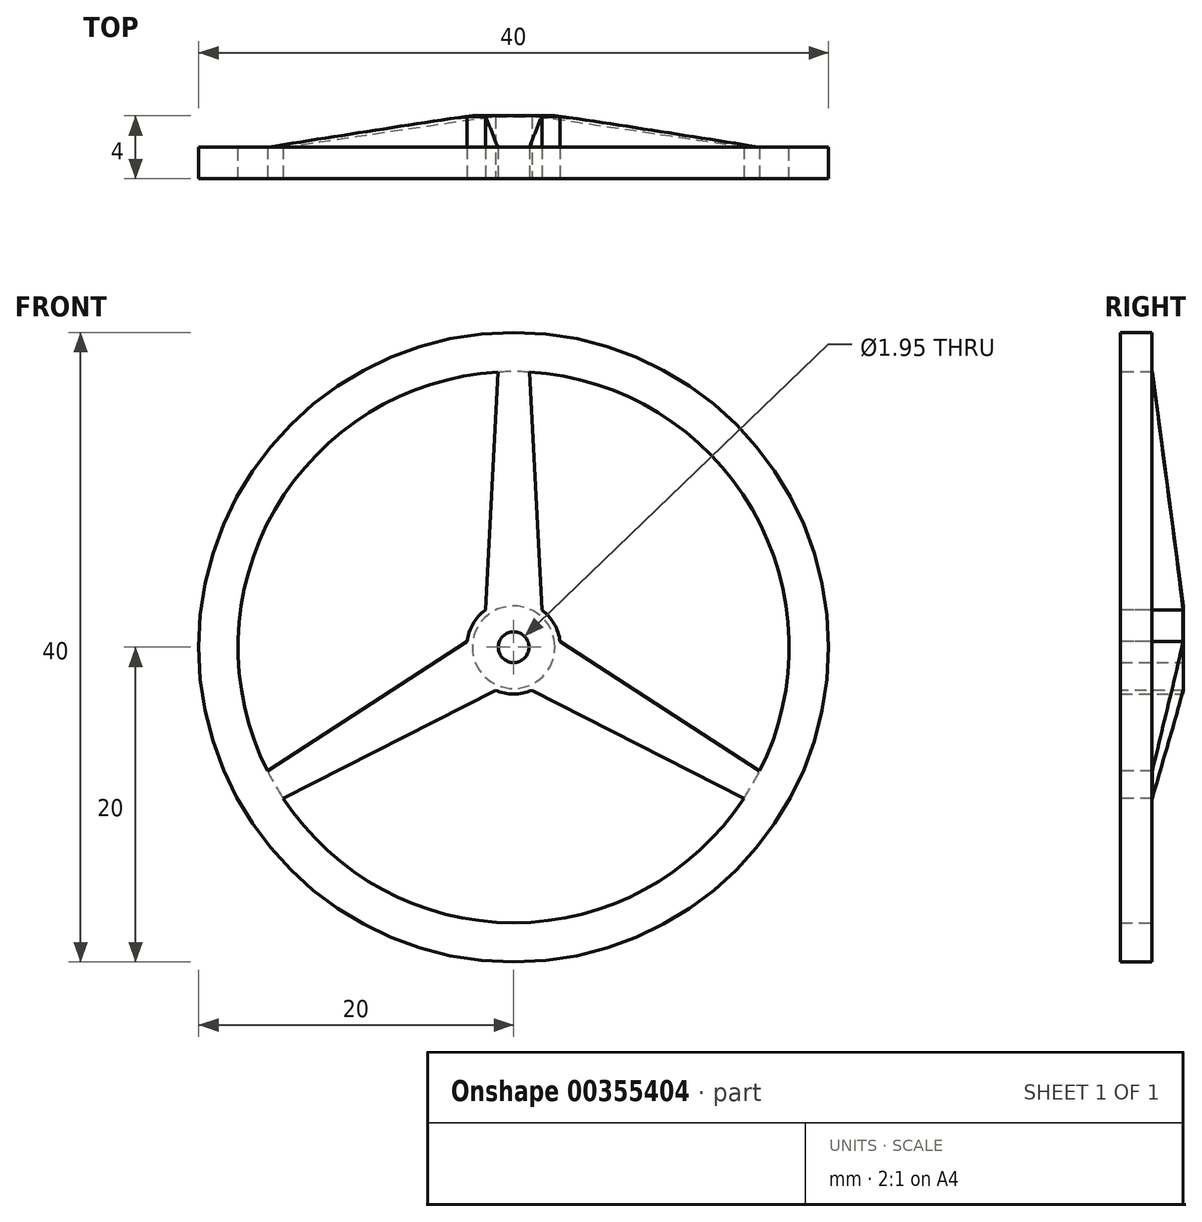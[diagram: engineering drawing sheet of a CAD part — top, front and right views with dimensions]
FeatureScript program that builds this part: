
annotation { "Feature Type Name" : "Feature", "Feature Type Description" : "" }
export const myFeature = defineFeature(function(context is Context, id is Id, definition is map)
    precondition{}
    {
        {
            var Q0;
            Q0=qCreatedBy(makeId("Front.planeOp"),FACE);
            var sketch = newSketch(context, id + "F0", { "sketchPlane" : qUnion([Q0])});
            skCircle(sketch, "E0", {"center": v(0, 0) * mm, "radius": 20 * mm});
            skCircle(sketch, "E1", {"center": v(0, 0) * mm, "radius": 0.97 * mm});
            skCircle(sketch, "E2", {"center": v(0, 0) * mm, "radius": 2.98 * mm});
            skCircle(sketch, "E3", {"center": v(0, 0) * mm, "radius": 17.5 * mm});
            skSolve(sketch);
        }
        {
            var Q0;
            Q0=qSketchRegion(id+"F0",true);
            var Q1;
            Q1=makeQuery(id+"F0.imprint","IMPRINT",FACE,{"disambiguationData":[TD([[makeQuery(id+"F0.imprint","IMPRINT",EDGE,{"derivedFrom":sQuery(id+"F0.wireOp",EDGE,"E1")}),-1.0]])]});
            extrude(context, id + "F1", {"entities" : qUnion([Q0, Q1]), "depth" : 2 * mm});
        }
        {
            var Q0;
            Q0=makeQuery(id+"F1.opExtrude","CAP_FACE",FACE,{"disambiguationData":[OSD([sQuery(id+"F0.wireOp",EDGE,"E0"),sQuery(id+"F0.wireOp",EDGE,"E3")])],"isStart":false});
            var sketch = newSketch(context, id + "F2", { "sketchPlane" : qUnion([Q0])});
            skLineSegment(sketch, "E4", {"start": v(1, 17.47) * mm, "end": v(1.8, 2.38) * mm});
            skLineSegment(sketch, "E5", {"start": v(-1, 17.47) * mm, "end": v(-1.8, 2.38) * mm});
            skLineSegment(sketch, "E6.1.0", {"start": v(-14.63, -9.6) * mm, "end": v(-1.16, -2.74) * mm});
            skLineSegment(sketch, "E6.1.1", {"start": v(-15.63, -7.87) * mm, "end": v(-2.95, 0.36) * mm});
            skLineSegment(sketch, "E6.2.0", {"start": v(15.63, -7.87) * mm, "end": v(2.95, 0.36) * mm});
            skLineSegment(sketch, "E6.2.1", {"start": v(14.63, -9.6) * mm, "end": v(1.16, -2.74) * mm});
            skPoint(sketch, "E6.center", {"position": v(0, 0) * mm});
            skArc(sketch, "E7", {"start": v(-15.63, -7.87) * mm, "mid": v(-15.16, -8.75) * mm, "end": v(-14.63, -9.6) * mm});
            skCircle(sketch, "E8", {"center": v(0, 0) * mm, "radius": 2.97 * mm});
            skArc(sketch, "E9.trimOffspring", {"start": v(1, 17.47) * mm, "mid": v(0, 17.5) * mm, "end": v(-1, 17.47) * mm});
            skArc(sketch, "E10.trimOffspring", {"start": v(14.63, -9.6) * mm, "mid": v(15.16, -8.75) * mm, "end": v(15.63, -7.87) * mm});
            skCircle(sketch, "E11", {"center": v(0, 0) * mm, "radius": 0.97 * mm});
            skSolve(sketch);
        }
        {
            var Q0;
            Q0 = qSketchRegion(id + "F2", true);
            extrude(context, id + "F3", {"entities" : qUnion([Q0]), "operationType" : NewBodyOperationType.ADD, "oppositeDirection" : true, "depth" : 4 * mm});
        }
        {
            var Q0;
            Q0=qCreatedBy(makeId("Right.planeOp"),FACE);
            var sketch = newSketch(context, id + "F4", { "sketchPlane" : qUnion([Q0])});
            skLineSegment(sketch, "E12", {"start": v(0, 17.54) * mm, "end": v(2.14, 1.57) * mm});
            skLineSegment(sketch, "E13", {"start": v(2.14, 1.57) * mm, "end": v(5.63, 1.57) * mm});
            skLineSegment(sketch, "E14", {"start": v(5.63, 1.57) * mm, "end": v(5.63, 19) * mm});
            skLineSegment(sketch, "E15", {"start": v(5.63, 19) * mm, "end": v(0, 19) * mm});
            skLineSegment(sketch, "E16", {"start": v(0, 19) * mm, "end": v(0, 17.54) * mm});
            skLineSegment(sketch, "E17", {"start": v(-16.5, 0) * mm, "end": v(18.02, 0) * mm});
            skLineSegment(sketch, "E18", {"start": v(18.02, 0) * mm, "end": v(18.02, 0.48) * mm});
            skSolve(sketch);
        }
        {
            var Q0;
            Q0 = qSketchRegion(id + "F4", true);
            var Q1;
            Q1=sQuery(id+"F4.wireOp",EDGE,"E17");
            revolve(context, id + "F5", {"operationType" : NewBodyOperationType.REMOVE, "entities" : qUnion([Q0]), "axis" : qUnion([Q1]), "revolveType" : RevolveType.FULL});
        }
    });
